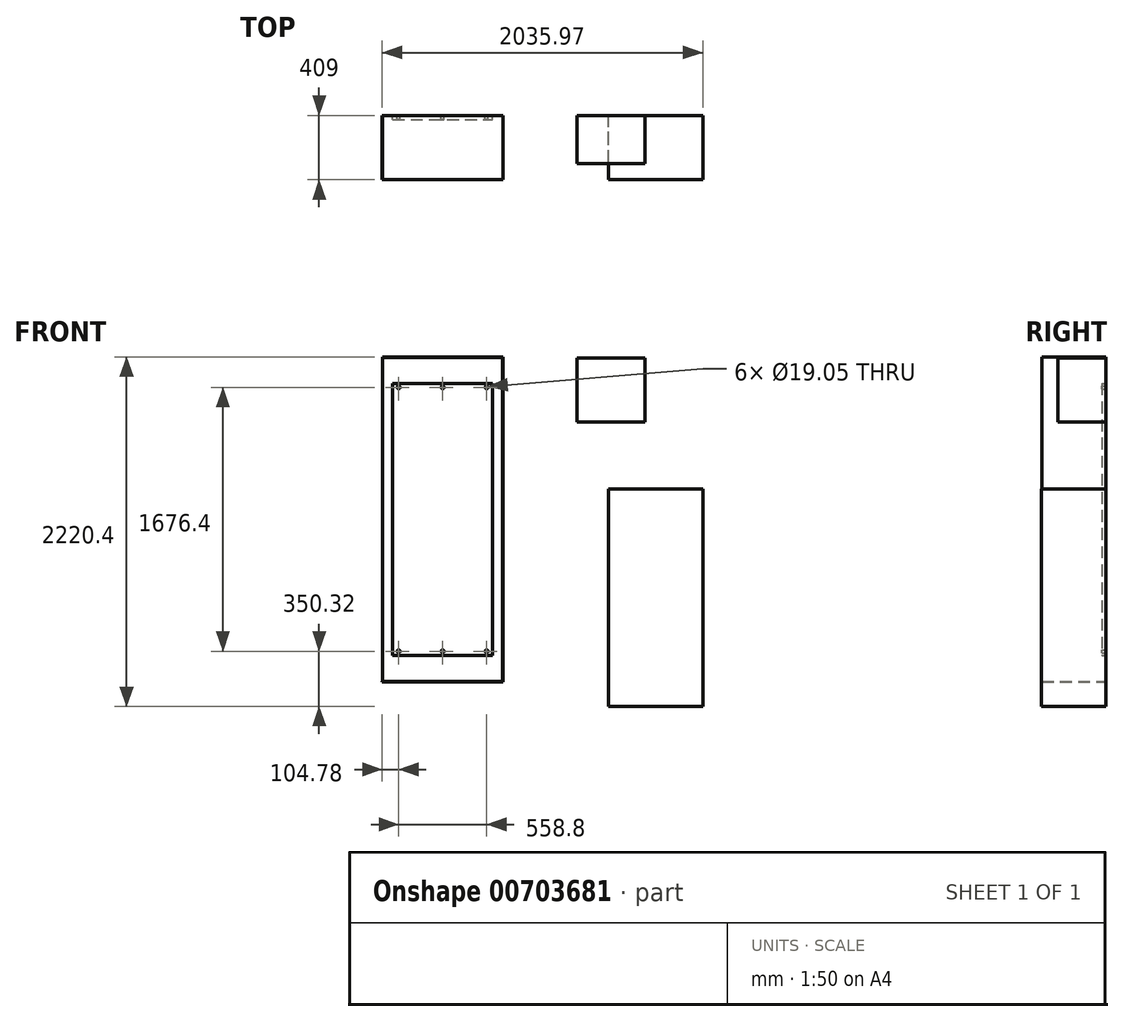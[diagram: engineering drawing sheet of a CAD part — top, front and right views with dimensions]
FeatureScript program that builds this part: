
annotation { "Feature Type Name" : "Feature", "Feature Type Description" : "" }
export const myFeature = defineFeature(function(context is Context, id is Id, definition is map)
    precondition{}
    {
        {
            var Q0;
            Q0=qCreatedBy(makeId("Front.planeOp"),FACE);
            var sketch = newSketch(context, id + "F0", { "sketchPlane" : qUnion([Q0])});
            skLineSegment(sketch, "E0.bottom", {"start": v(-381, 1028.7) * mm, "end": v(381, 1028.7) * mm});
            skLineSegment(sketch, "E0.top", {"start": v(-381, -1028.7) * mm, "end": v(381, -1028.7) * mm});
            skLineSegment(sketch, "E0.left", {"start": v(-381, 1028.7) * mm, "end": v(-381, -1028.7) * mm});
            skLineSegment(sketch, "E0.right", {"start": v(381, 1028.7) * mm, "end": v(381, -1028.7) * mm});
            skPoint(sketch, "E0.middle", {"position": v(0, 0) * mm});
            skLineSegment(sketch, "E1.top", {"start": v(-381, 1031.88) * mm, "end": v(381, 1031.88) * mm});
            skLineSegment(sketch, "E1.left", {"start": v(-381, 1028.7) * mm, "end": v(-381, 1031.88) * mm});
            skLineSegment(sketch, "E1.right", {"start": v(381, 1028.7) * mm, "end": v(381, 1031.88) * mm});
            skLineSegment(sketch, "E2.top", {"start": v(381, -1028.7) * mm, "end": v(384.18, -1028.7) * mm});
            skLineSegment(sketch, "E2.right", {"start": v(384.18, 1031.88) * mm, "end": v(384.18, -1028.7) * mm});
            skLineSegment(sketch, "E3.bottom", {"start": v(384.18, -1028.7) * mm, "end": v(-384.18, -1028.7) * mm});
            skLineSegment(sketch, "E3.top", {"start": v(384.18, -1031.87) * mm, "end": v(-384.18, -1031.87) * mm});
            skLineSegment(sketch, "E3.left", {"start": v(384.18, -1028.7) * mm, "end": v(384.18, -1031.87) * mm});
            skLineSegment(sketch, "E3.right", {"start": v(-384.18, -1028.7) * mm, "end": v(-384.18, -1031.87) * mm});
            skLineSegment(sketch, "E4.bottom", {"start": v(-384.18, -1028.7) * mm, "end": v(-381, -1028.7) * mm});
            skLineSegment(sketch, "E4.top", {"start": v(-384.18, 1031.88) * mm, "end": v(-381, 1031.88) * mm});
            skLineSegment(sketch, "E4.left", {"start": v(-384.18, -1028.7) * mm, "end": v(-384.18, 1031.88) * mm});
            skLineSegment(sketch, "E4.right", {"start": v(-381, -1028.7) * mm, "end": v(-381, 1031.88) * mm});
            skLineSegment(sketch, "E5", {"start": v(384.18, 1031.88) * mm, "end": v(381, 1031.88) * mm});
            skSolve(sketch);
        }
        {
            var Q0;
            Q0=makeQuery(id+"F0.imprint","IMPRINT",FACE,{"disambiguationData":[TD([[makeQuery(id+"F0.imprint","IMPRINT",EDGE,{"derivedFrom":sQuery(id+"F0.wireOp",EDGE,"E3.top")}),-1.0]])]});
            var Q1;
            {var subQ2=sQuery(id+"F0.wireOp",EDGE,"E4.bottom");Q1=makeQuery(id+"F0.imprint","IMPRINT",FACE,{"disambiguationData":[TD([[makeQuery(id+"F0.imprint","IMPRINT",EDGE,{"derivedFrom":subQ2}),1.0]])]});}
            var Q2;
            Q2=makeQuery(id+"F0.imprint","IMPRINT",FACE,{"disambiguationData":[TD([[makeQuery(id+"F0.imprint","IMPRINT",EDGE,{"derivedFrom":sQuery(id+"F0.wireOp",EDGE,"E1.right")}),-1.0]])]});
            var Q3;
            {var subQ0=sQuery(id+"F0.wireOp",EDGE,"E0.bottom");Q3=makeQuery(id+"F0.imprint","IMPRINT",FACE,{"disambiguationData":[TD([[makeQuery(id+"F0.imprint","IMPRINT",EDGE,{"derivedFrom":subQ0}),1.0]])]});}
            var Q4;
            {var subQ0=sQuery(id+"F0.wireOp",EDGE,"E0.bottom");Q4=makeQuery(id+"F0.imprint","IMPRINT",FACE,{"disambiguationData":[TD([[makeQuery(id+"F0.imprint","IMPRINT",EDGE,{"derivedFrom":subQ0}),-1.0]])]});}
            extrude(context, id + "F1", {"entities" : qUnion([Q0, Q1, Q2, Q3, Q4]), "depth" : 1 / 203.2 * mm, "offsetDistance" : 25 * mm});
        }
        {
            var Q0;
            {var subQ2=sQuery(id+"F0.wireOp",EDGE,"E4.bottom");Q0=makeQuery(id+"F0.imprint","IMPRINT",FACE,{"disambiguationData":[TD([[makeQuery(id+"F0.imprint","IMPRINT",EDGE,{"derivedFrom":subQ2}),1.0]])]});}
            var Q1;
            {var subQ0=sQuery(id+"F0.wireOp",EDGE,"E0.bottom");Q1=makeQuery(id+"F0.imprint","IMPRINT",FACE,{"disambiguationData":[TD([[makeQuery(id+"F0.imprint","IMPRINT",EDGE,{"derivedFrom":subQ0}),1.0]])]});}
            var Q2;
            Q2=makeQuery(id+"F0.imprint","IMPRINT",FACE,{"disambiguationData":[TD([[makeQuery(id+"F0.imprint","IMPRINT",EDGE,{"derivedFrom":sQuery(id+"F0.wireOp",EDGE,"E1.right")}),-1.0]])]});
            var Q3;
            Q3=makeQuery(id+"F0.imprint","IMPRINT",FACE,{"disambiguationData":[TD([[makeQuery(id+"F0.imprint","IMPRINT",EDGE,{"derivedFrom":sQuery(id+"F0.wireOp",EDGE,"E3.top")}),-1.0]])]});
            extrude(context, id + "F2", {"entities" : qUnion([Q0, Q1, Q2, Q3]), "operationType" : NewBodyOperationType.ADD, "depth" : 406.4 * mm, "offsetDistance" : 25 * mm});
        }
        {
            var Q0;
            Q0=makeQuery(id+"F1.opExtrude","CAP_FACE",FACE,{"disambiguationData":[OSD([sQuery(id+"F0.wireOp",EDGE,"E1.top"),sQuery(id+"F0.wireOp",EDGE,"E2.right"),sQuery(id+"F0.wireOp",EDGE,"E3.top"),sQuery(id+"F0.wireOp",EDGE,"E3.left"),sQuery(id+"F0.wireOp",EDGE,"E3.right"),sQuery(id+"F0.wireOp",EDGE,"E4.top"),sQuery(id+"F0.wireOp",EDGE,"E4.left"),sQuery(id+"F0.wireOp",EDGE,"E5")])],"isStart":false});
            var sketch = newSketch(context, id + "F3", { "sketchPlane" : qUnion([Q0])});
            skLineSegment(sketch, "E6.bottom", {"start": v(-317.5, 863.6) * mm, "end": v(317.5, 863.6) * mm});
            skLineSegment(sketch, "E6.top", {"start": v(-317.5, -863.6) * mm, "end": v(317.5, -863.6) * mm});
            skLineSegment(sketch, "E6.left", {"start": v(-317.5, 863.6) * mm, "end": v(-317.5, -863.6) * mm});
            skLineSegment(sketch, "E6.right", {"start": v(317.5, 863.6) * mm, "end": v(317.5, -863.6) * mm});
            skPoint(sketch, "E6.middle", {"position": v(0, 0) * mm});
            skPoint(sketch, "E7", {"position": v(0, 863.6) * mm});
            skLineSegment(sketch, "E8.top", {"start": v(-381, -800.1) * mm, "end": v(381, -800.1) * mm});
            skCircle(sketch, "E9", {"center": v(-279.4, 838.2) * mm, "radius": 9.53 * mm});
            skCircle(sketch, "E10", {"center": v(0, 838.2) * mm, "radius": 9.53 * mm});
            skCircle(sketch, "E11", {"center": v(279.4, 838.2) * mm, "radius": 9.53 * mm});
            skCircle(sketch, "E12", {"center": v(-279.4, -838.2) * mm, "radius": 9.53 * mm});
            skCircle(sketch, "E13", {"center": v(0, -838.2) * mm, "radius": 9.53 * mm});
            skCircle(sketch, "E14", {"center": v(279.4, -838.2) * mm, "radius": 9.53 * mm});
            skLineSegment(sketch, "E15", {"start": v(381, 762) * mm, "end": v(-381, 762) * mm});
            skLineSegment(sketch, "E16.bottom", {"start": v(851.98, 1023.26) * mm, "end": v(1283.78, 1023.26) * mm});
            skLineSegment(sketch, "E16.top", {"start": v(851.98, 616.86) * mm, "end": v(1283.78, 616.86) * mm});
            skLineSegment(sketch, "E16.left", {"start": v(851.98, 1023.26) * mm, "end": v(851.98, 616.86) * mm});
            skLineSegment(sketch, "E16.right", {"start": v(1283.78, 1023.26) * mm, "end": v(1283.78, 616.86) * mm});
            skLineSegment(sketch, "E17.bottom", {"start": v(1051.8, 193.48) * mm, "end": v(1651.8, 193.48) * mm});
            skLineSegment(sketch, "E17.top", {"start": v(1051.8, -1188.52) * mm, "end": v(1651.8, -1188.52) * mm});
            skLineSegment(sketch, "E17.left", {"start": v(1051.8, 193.48) * mm, "end": v(1051.8, -1188.52) * mm});
            skLineSegment(sketch, "E17.right", {"start": v(1651.8, 193.48) * mm, "end": v(1651.8, -1188.52) * mm});
            skSolve(sketch);
        }
        {
            var Q0;
            {var subQ0=sQuery(id+"F3.wireOp",EDGE,"E6.bottom");Q0=makeQuery(id+"F3.imprint","IMPRINT",FACE,{"disambiguationData":[TD([[makeQuery(id+"F3.imprint","IMPRINT",EDGE,{"derivedFrom":subQ0}),-1.0]])]});}
            var Q1;
            {var subQ0=sQuery(id+"F3.wireOp",EDGE,"E15");var subQ1=sQuery(id+"F3.wireOp",EDGE,"E6.left");var subQ2=makeQuery(id+"F3.imprint","INTERSECT",VERTEX,{"derivedFrom":[subQ1,subQ0]});Q1=makeQuery(id+"F3.imprint","IMPRINT",FACE,{"disambiguationData":[TD([[makeQuery(id+"F3.imprint","IMPRINT",EDGE,{"disambiguationData":[TD([[subQ2,-1.0]])],"derivedFrom":subQ1}),1.0]])]});}
            var Q2;
            {var subQ1=sQuery(id+"F3.wireOp",EDGE,"E6.top");Q2=makeQuery(id+"F3.imprint","IMPRINT",FACE,{"disambiguationData":[TD([[makeQuery(id+"F3.imprint","IMPRINT",EDGE,{"derivedFrom":subQ1}),1.0]])]});}
            extrude(context, id + "F4", {"entities" : qUnion([Q0, Q1, Q2]), "depth" : 25.4 * mm, "offsetDistance" : 25 * mm, "hasSecondDirection" : true, "secondDirectionOppositeDirection" : false, "secondDirectionDepth" : 3 / 101.6 * mm});
        }
        {
            var Q0;
            Q0=makeQuery(id+"F3.imprint","IMPRINT",FACE,{"disambiguationData":[TD([[makeQuery(id+"F3.imprint","IMPRINT",EDGE,{"derivedFrom":sQuery(id+"F3.wireOp",EDGE,"E16.bottom")}),-1.0]])]});
            extrude(context, id + "F5", {"entities" : qUnion([Q0]), "depth" : 304.8 * mm, "offsetDistance" : 25 * mm});
        }
        {
            var Q0;
            Q0=makeQuery(id+"F3.imprint","IMPRINT",FACE,{"disambiguationData":[TD([[makeQuery(id+"F3.imprint","IMPRINT",EDGE,{"derivedFrom":sQuery(id+"F3.wireOp",EDGE,"E17.bottom")}),-1.0]])]});
            extrude(context, id + "F6", {"entities" : qUnion([Q0]), "depth" : 409 * mm, "offsetDistance" : 25 * mm});
        }
    });
